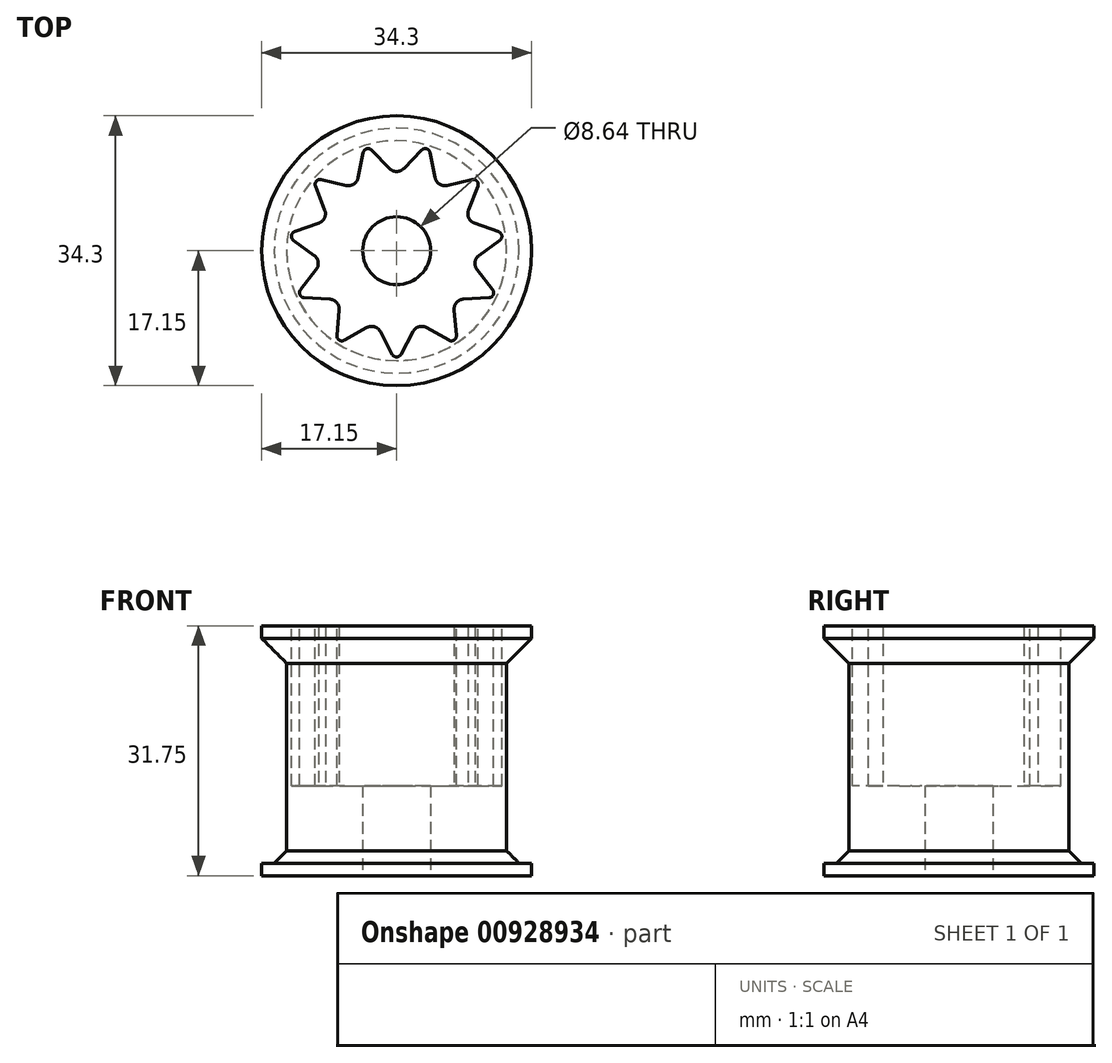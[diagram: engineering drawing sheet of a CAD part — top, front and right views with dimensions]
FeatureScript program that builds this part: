
annotation { "Feature Type Name" : "Feature", "Feature Type Description" : "" }
export const myFeature = defineFeature(function(context is Context, id is Id, definition is map)
    precondition{}
    {
        {
            var Q0;
            Q0=qCreatedBy(makeId("Top.planeOp"),FACE);
            var sketch = newSketch(context, id + "F0", { "sketchPlane" : qUnion([Q0])});
            skCircle(sketch, "E0", {"center": v(0, 0) * mm, "radius": 4.32 * mm});
            skCircle(sketch, "E1", {"center": v(0, 0) * mm, "radius": 12.7 * mm});
            skSolve(sketch);
        }
        {
            var Q0;
            Q0=makeQuery(id+"F0.imprint","IMPRINT",FACE,{"disambiguationData":[TD([[makeQuery(id+"F0.imprint","IMPRINT",EDGE,{"derivedFrom":sQuery(id+"F0.wireOp",EDGE,"E0")}),-1.0]])]});
            extrude(context, id + "F1", {"entities" : qUnion([Q0]), "depth" : 11.43 * mm, "offsetDistance" : 25.4 * mm});
        }
        {
            var Q0;
            Q0=qCreatedBy(makeId("Front.planeOp"),FACE);
            var sketch = newSketch(context, id + "F2", { "sketchPlane" : qUnion([Q0])});
            skLineSegment(sketch, "E2.bottom", {"start": v(0, 0) * mm, "end": v(-17.15, 0) * mm});
            skLineSegment(sketch, "E2.top", {"start": v(0, 0) * mm, "end": v(-17.15, 0) * mm});
            skLineSegment(sketch, "E2.left", {"start": v(0, 0) * mm, "end": v(0, 0) * mm});
            skLineSegment(sketch, "E2.right", {"start": v(-17.15, 0) * mm, "end": v(-17.15, 0) * mm});
            skLineSegment(sketch, "E3.top", {"start": v(-17.15, 1.59) * mm, "end": v(-17.15, 1.59) * mm});
            skLineSegment(sketch, "E3.left", {"start": v(-17.15, 0) * mm, "end": v(-17.15, 1.59) * mm});
            skLineSegment(sketch, "E3.right", {"start": v(-17.15, 0) * mm, "end": v(-17.15, 1.59) * mm});
            skLineSegment(sketch, "E4", {"start": v(-17.15, 1.59) * mm, "end": v(-13.97, 1.59) * mm});
            skLineSegment(sketch, "E5", {"start": v(-13.97, 1.59) * mm, "end": v(-13.97, 30.16) * mm});
            skLineSegment(sketch, "E6", {"start": v(-13.97, 30.16) * mm, "end": v(-17.15, 30.16) * mm});
            skLineSegment(sketch, "E7", {"start": v(-17.15, 30.16) * mm, "end": v(-17.15, 31.75) * mm});
            skLineSegment(sketch, "E8", {"start": v(-17.15, 31.75) * mm, "end": v(-10.8, 31.75) * mm});
            skLineSegment(sketch, "E9", {"start": v(0, 0) * mm, "end": v(-7.62, 0) * mm});
            skLineSegment(sketch, "E10", {"start": v(-7.62, 0) * mm, "end": v(-7.62, 1.59) * mm});
            skLineSegment(sketch, "E11", {"start": v(-7.62, 1.59) * mm, "end": v(-10.8, 1.59) * mm});
            skLineSegment(sketch, "E12", {"start": v(-10.8, 31.75) * mm, "end": v(-10.8, 1.59) * mm});
            skLineSegment(sketch, "E13", {"start": v(-17.15, 30.16) * mm, "end": v(-13.97, 26.99) * mm});
            skLineSegment(sketch, "E14", {"start": v(0, 0) * mm, "end": v(0, 23.16) * mm});
            skSolve(sketch);
        }
        {
            var Q0;
            {var subQ5=sQuery(id+"F2.wireOp",EDGE,"E3.left");Q0=makeQuery(id+"F2.imprint","IMPRINT",FACE,{"disambiguationData":[TD([[makeQuery(id+"F2.imprint","IMPRINT",EDGE,{"derivedFrom":subQ5}),-1.0]])]});}
            var Q1;
            {var subQ0=sQuery(id+"F2.wireOp",EDGE,"E6");Q1=makeQuery(id+"F2.imprint","IMPRINT",FACE,{"disambiguationData":[TD([[makeQuery(id+"F2.imprint","IMPRINT",EDGE,{"derivedFrom":subQ0}),1.0]])]});}
            var Q2;
            Q2=sQuery(id+"F2.wireOp",EDGE,"E14");
            revolve(context, id + "F3", {"operationType" : NewBodyOperationType.ADD, "surfaceOperationType" : NewSurfaceOperationType.NEW, "entities" : qUnion([Q0, Q1]), "axis" : qUnion([Q2]), "revolveType" : RevolveType.FULL});
        }
        {
            var Q0;
            Q0=makeQuery(id+"F1.opExtrude","CAP_FACE",FACE,{"disambiguationData":[OSD([sQuery(id+"F0.wireOp",EDGE,"E0"),sQuery(id+"F0.wireOp",EDGE,"E1")])],"isStart":false});
            var sketch = newSketch(context, id + "F4", { "sketchPlane" : qUnion([Q0])});
            skCircle(sketch, "E15", {"center": v(0, 0) * mm, "radius": 13.5 * mm});
            skLineSegment(sketch, "E16", {"start": v(0, 13.5) * mm, "end": v(0, 10.06) * mm});
            skArc(sketch, "E17", {"start": v(-0.91, 10.45) * mm, "mid": v(0, 10.06) * mm, "end": v(0.91, 10.45) * mm});
            skArc(sketch, "E18.1.0", {"start": v(-6.42, 8.3) * mm, "mid": v(-5.44, 8.47) * mm, "end": v(-4.88, 9.29) * mm});
            skArc(sketch, "E18.2.0", {"start": v(-9.89, 3.51) * mm, "mid": v(-9.16, 4.18) * mm, "end": v(-9.13, 5.17) * mm});
            skArc(sketch, "E18.3.0", {"start": v(-10.22, -2.4) * mm, "mid": v(-9.96, -1.43) * mm, "end": v(-10.47, -0.58) * mm});
            skArc(sketch, "E18.4.0", {"start": v(-7.3, -7.53) * mm, "mid": v(-7.6, -6.6) * mm, "end": v(-8.5, -6.15) * mm});
            skArc(sketch, "E18.5.0", {"start": v(-2.07, -10.29) * mm, "mid": v(-2.84, -9.66) * mm, "end": v(-3.82, -9.77) * mm});
            skArc(sketch, "E18.6.0", {"start": v(3.82, -9.77) * mm, "mid": v(2.84, -9.66) * mm, "end": v(2.07, -10.29) * mm});
            skArc(sketch, "E18.7.0", {"start": v(8.5, -6.15) * mm, "mid": v(7.6, -6.6) * mm, "end": v(7.3, -7.53) * mm});
            skArc(sketch, "E18.8.0", {"start": v(10.47, -0.58) * mm, "mid": v(9.96, -1.43) * mm, "end": v(10.22, -2.4) * mm});
            skArc(sketch, "E18.9.0", {"start": v(9.13, 5.17) * mm, "mid": v(9.16, 4.18) * mm, "end": v(9.89, 3.51) * mm});
            skArc(sketch, "E18.10.0", {"start": v(4.88, 9.29) * mm, "mid": v(5.44, 8.47) * mm, "end": v(6.42, 8.3) * mm});
            skLineSegment(sketch, "E19", {"start": v(0, 0) * mm, "end": v(3.8, 12.95) * mm});
            skCircle(sketch, "E20", {"center": v(3.62, 12.34) * mm, "radius": 0.64 * mm});
            skCircle(sketch, "E21.1.0", {"center": v(-3.62, 12.34) * mm, "radius": 0.64 * mm});
            skCircle(sketch, "E21.2.0", {"center": v(-9.72, 8.42) * mm, "radius": 0.64 * mm});
            skCircle(sketch, "E22.1.3.0", {"center": v(-12.73, 1.83) * mm, "radius": 0.64 * mm});
            skCircle(sketch, "E22.1.4.0", {"center": v(-11.7, -5.34) * mm, "radius": 0.64 * mm});
            skCircle(sketch, "E22.1.5.0", {"center": v(-6.95, -10.82) * mm, "radius": 0.64 * mm});
            skCircle(sketch, "E22.1.6.0", {"center": v(0, -12.86) * mm, "radius": 0.64 * mm});
            skCircle(sketch, "E22.1.7.0", {"center": v(6.95, -10.82) * mm, "radius": 0.64 * mm});
            skCircle(sketch, "E22.1.8.0", {"center": v(11.7, -5.34) * mm, "radius": 0.64 * mm});
            skCircle(sketch, "E22.1.9.0", {"center": v(12.73, 1.83) * mm, "radius": 0.64 * mm});
            skCircle(sketch, "E22.1.10.0", {"center": v(9.72, 8.42) * mm, "radius": 0.64 * mm});
            skLineSegment(sketch, "E23", {"start": v(-9.13, 5.17) * mm, "end": v(-10.3, 8.19) * mm});
            skLineSegment(sketch, "E24", {"start": v(-9.89, 3.51) * mm, "end": v(-12.94, 2.43) * mm});
            skLineSegment(sketch, "E25", {"start": v(-9.57, 9.04) * mm, "end": v(-6.42, 8.3) * mm});
            skLineSegment(sketch, "E26", {"start": v(-13.1, 1.32) * mm, "end": v(-10.47, -0.58) * mm});
            skLineSegment(sketch, "E27", {"start": v(-10.22, -2.4) * mm, "end": v(-12.2, -4.95) * mm});
            skLineSegment(sketch, "E28", {"start": v(-7.3, -7.53) * mm, "end": v(-7.58, -10.76) * mm});
            skLineSegment(sketch, "E29", {"start": v(-6.64, -11.37) * mm, "end": v(-3.82, -9.77) * mm});
            skLineSegment(sketch, "E30", {"start": v(-2.07, -10.29) * mm, "end": v(-0.56, -13.15) * mm});
            skLineSegment(sketch, "E31", {"start": v(0.56, -13.15) * mm, "end": v(2.07, -10.29) * mm});
            skLineSegment(sketch, "E32", {"start": v(3.82, -9.77) * mm, "end": v(6.64, -11.37) * mm});
            skLineSegment(sketch, "E33", {"start": v(7.58, -10.76) * mm, "end": v(7.3, -7.53) * mm});
            skLineSegment(sketch, "E34", {"start": v(8.5, -6.15) * mm, "end": v(11.73, -5.98) * mm});
            skLineSegment(sketch, "E35", {"start": v(-4.88, 9.29) * mm, "end": v(-4.25, 12.46) * mm});
            skLineSegment(sketch, "E36", {"start": v(-3.17, 12.78) * mm, "end": v(-0.91, 10.45) * mm});
            skLineSegment(sketch, "E37", {"start": v(0.91, 10.45) * mm, "end": v(3.17, 12.78) * mm});
            skLineSegment(sketch, "E38", {"start": v(10.3, 8.19) * mm, "end": v(9.13, 5.17) * mm});
            skLineSegment(sketch, "E39", {"start": v(9.89, 3.51) * mm, "end": v(12.94, 2.43) * mm});
            skLineSegment(sketch, "E40", {"start": v(13.1, 1.32) * mm, "end": v(10.47, -0.58) * mm});
            skLineSegment(sketch, "E41", {"start": v(10.22, -2.4) * mm, "end": v(12.2, -4.95) * mm});
            skLineSegment(sketch, "E42", {"start": v(4.25, 12.46) * mm, "end": v(4.88, 9.29) * mm});
            skLineSegment(sketch, "E43", {"start": v(6.42, 8.3) * mm, "end": v(9.57, 9.04) * mm});
            skLineSegment(sketch, "E44", {"start": v(-11.73, -5.98) * mm, "end": v(-8.5, -6.15) * mm});
            skCircle(sketch, "E45", {"center": v(0, 0) * mm, "radius": 15.88 * mm});
            skSolve(sketch);
        }
        {
            var Q0;
            Q0=makeQuery(id+"F3.opRevolve","SWEPT_EDGE",EDGE,{"disambiguationData":[OSD([sQuery(id+"F2.wireOp",EDGE,"E4"),sQuery(id+"F2.wireOp",EDGE,"E5")])]});
            chamfer(context, id + "F5", {"entities" : qUnion([Q0]), "width" : 1.59 * mm, "tangentPropagation" : true});
        }
        {
            var Q0;
            Q0=makeQuery(id+"F3.opRevolve","SWEPT_FACE",FACE,{"disambiguationData":[OSD([sQuery(id+"F2.wireOp",EDGE,"E8")])]});
            var sketch = newSketch(context, id + "F6", { "sketchPlane" : qUnion([Q0])});
            skCircle(sketch, "E46", {"center": v(0, 0) * mm, "radius": 13.5 * mm});
            skLineSegment(sketch, "E47", {"start": v(0, 13.5) * mm, "end": v(0, 10.06) * mm});
            skCircle(sketch, "E48", {"center": v(0, 11.33) * mm, "radius": 1.27 * mm});
            skCircle(sketch, "E49.1.0", {"center": v(-6.13, 9.54) * mm, "radius": 1.27 * mm});
            skCircle(sketch, "E49.2.0", {"center": v(-10.31, 4.7) * mm, "radius": 1.27 * mm});
            skCircle(sketch, "E49.3.0", {"center": v(-11.22, -1.61) * mm, "radius": 1.27 * mm});
            skCircle(sketch, "E49.4.0", {"center": v(-8.57, -7.42) * mm, "radius": 1.27 * mm});
            skCircle(sketch, "E49.5.0", {"center": v(-3.2, -10.88) * mm, "radius": 1.27 * mm});
            skCircle(sketch, "E49.6.0", {"center": v(3.2, -10.88) * mm, "radius": 1.27 * mm});
            skCircle(sketch, "E49.7.0", {"center": v(8.57, -7.42) * mm, "radius": 1.27 * mm});
            skCircle(sketch, "E49.8.0", {"center": v(11.22, -1.61) * mm, "radius": 1.27 * mm});
            skCircle(sketch, "E49.9.0", {"center": v(10.31, 4.7) * mm, "radius": 1.27 * mm});
            skCircle(sketch, "E49.10.0", {"center": v(6.13, 9.54) * mm, "radius": 1.27 * mm});
            skLineSegment(sketch, "E50", {"start": v(0, 0) * mm, "end": v(3.8, 12.95) * mm});
            skCircle(sketch, "E51", {"center": v(3.62, 12.34) * mm, "radius": 0.64 * mm});
            skCircle(sketch, "E52.1.0", {"center": v(-3.62, 12.34) * mm, "radius": 0.64 * mm});
            skCircle(sketch, "E52.2.0", {"center": v(-9.72, 8.42) * mm, "radius": 0.64 * mm});
            skCircle(sketch, "E53.1.3.0", {"center": v(-12.73, 1.83) * mm, "radius": 0.64 * mm});
            skCircle(sketch, "E53.1.4.0", {"center": v(-11.7, -5.34) * mm, "radius": 0.64 * mm});
            skCircle(sketch, "E53.1.5.0", {"center": v(-6.95, -10.82) * mm, "radius": 0.64 * mm});
            skCircle(sketch, "E53.1.6.0", {"center": v(0, -12.86) * mm, "radius": 0.64 * mm});
            skCircle(sketch, "E53.1.7.0", {"center": v(6.95, -10.82) * mm, "radius": 0.64 * mm});
            skCircle(sketch, "E53.1.8.0", {"center": v(11.7, -5.34) * mm, "radius": 0.64 * mm});
            skCircle(sketch, "E53.1.9.0", {"center": v(12.73, 1.83) * mm, "radius": 0.64 * mm});
            skCircle(sketch, "E53.1.10.0", {"center": v(9.72, 8.42) * mm, "radius": 0.64 * mm});
            skLineSegment(sketch, "E54", {"start": v(-9.13, 5.17) * mm, "end": v(-10.3, 8.19) * mm});
            skLineSegment(sketch, "E55", {"start": v(-9.89, 3.51) * mm, "end": v(-12.94, 2.43) * mm});
            skLineSegment(sketch, "E56", {"start": v(-9.57, 9.04) * mm, "end": v(-6.42, 8.3) * mm});
            skLineSegment(sketch, "E57", {"start": v(-13.1, 1.32) * mm, "end": v(-10.47, -0.58) * mm});
            skLineSegment(sketch, "E58", {"start": v(-10.22, -2.4) * mm, "end": v(-12.2, -4.95) * mm});
            skLineSegment(sketch, "E59", {"start": v(-7.3, -7.53) * mm, "end": v(-7.58, -10.76) * mm});
            skLineSegment(sketch, "E60", {"start": v(-6.64, -11.37) * mm, "end": v(-3.82, -9.77) * mm});
            skLineSegment(sketch, "E61", {"start": v(-2.07, -10.29) * mm, "end": v(-0.56, -13.15) * mm});
            skLineSegment(sketch, "E62", {"start": v(0.56, -13.15) * mm, "end": v(2.07, -10.29) * mm});
            skLineSegment(sketch, "E63", {"start": v(3.82, -9.77) * mm, "end": v(6.64, -11.37) * mm});
            skLineSegment(sketch, "E64", {"start": v(7.58, -10.76) * mm, "end": v(7.3, -7.53) * mm});
            skLineSegment(sketch, "E65", {"start": v(8.5, -6.15) * mm, "end": v(11.73, -5.98) * mm});
            skLineSegment(sketch, "E66", {"start": v(-4.88, 9.29) * mm, "end": v(-4.25, 12.46) * mm});
            skLineSegment(sketch, "E67", {"start": v(-3.17, 12.78) * mm, "end": v(-0.91, 10.45) * mm});
            skLineSegment(sketch, "E68", {"start": v(0.91, 10.45) * mm, "end": v(3.17, 12.78) * mm});
            skLineSegment(sketch, "E69", {"start": v(10.3, 8.19) * mm, "end": v(9.13, 5.17) * mm});
            skLineSegment(sketch, "E70", {"start": v(9.89, 3.51) * mm, "end": v(12.94, 2.43) * mm});
            skLineSegment(sketch, "E71", {"start": v(13.1, 1.32) * mm, "end": v(10.47, -0.58) * mm});
            skLineSegment(sketch, "E72", {"start": v(10.22, -2.4) * mm, "end": v(12.2, -4.95) * mm});
            skLineSegment(sketch, "E73", {"start": v(4.25, 12.46) * mm, "end": v(4.88, 9.29) * mm});
            skLineSegment(sketch, "E74", {"start": v(6.42, 8.3) * mm, "end": v(9.57, 9.04) * mm});
            skLineSegment(sketch, "E75", {"start": v(-11.73, -5.98) * mm, "end": v(-8.5, -6.15) * mm});
            skCircle(sketch, "E76", {"center": v(0, 0) * mm, "radius": 15.88 * mm});
            skSolve(sketch);
        }
        {
            var Q0;
            {var subQ0=sQuery(id+"F6.wireOp",EDGE,"E58");var subQ1=sQuery(id+"F6.wireOp",EDGE,"E53.1.4.0");var subQ2=makeQuery(id+"F6.imprint","INTERSECT",VERTEX,{"derivedFrom":[subQ1,subQ0]});Q0=makeQuery(id+"F6.imprint","IMPRINT",FACE,{"disambiguationData":[TD([[makeQuery(id+"F6.imprint","IMPRINT",EDGE,{"disambiguationData":[TD([[subQ2,1.0]])],"derivedFrom":subQ1}),-1.0]])]});}
            var Q1;
            {var subQ0=sQuery(id+"F6.wireOp",EDGE,"E53.1.4.0");var subQ1=makeQuery(id+"F6.imprint","INTERSECT",VERTEX,{"derivedFrom":[subQ0,sQuery(id+"F6.wireOp",EDGE,"E58")]});Q1=makeQuery(id+"F6.imprint","IMPRINT",FACE,{"disambiguationData":[TD([[makeQuery(id+"F6.imprint","IMPRINT",EDGE,{"disambiguationData":[TD([[subQ1,-1.0]])],"derivedFrom":subQ0}),1.0]])]});}
            var Q2;
            {var subQ0=sQuery(id+"F6.wireOp",EDGE,"E55");var subQ1=sQuery(id+"F6.wireOp",EDGE,"E53.1.3.0");var subQ2=makeQuery(id+"F6.imprint","INTERSECT",VERTEX,{"derivedFrom":[subQ1,subQ0]});Q2=makeQuery(id+"F6.imprint","IMPRINT",FACE,{"disambiguationData":[TD([[makeQuery(id+"F6.imprint","IMPRINT",EDGE,{"disambiguationData":[TD([[subQ2,1.0]])],"derivedFrom":subQ1}),-1.0]])]});}
            var Q3;
            {var subQ0=sQuery(id+"F6.wireOp",EDGE,"E53.1.3.0");var subQ1=makeQuery(id+"F6.imprint","INTERSECT",VERTEX,{"derivedFrom":[subQ0,sQuery(id+"F6.wireOp",EDGE,"E55")]});Q3=makeQuery(id+"F6.imprint","IMPRINT",FACE,{"disambiguationData":[TD([[makeQuery(id+"F6.imprint","IMPRINT",EDGE,{"disambiguationData":[TD([[subQ1,-1.0]])],"derivedFrom":subQ0}),1.0]])]});}
            var Q4;
            {var subQ0=sQuery(id+"F6.wireOp",EDGE,"E54");var subQ1=sQuery(id+"F6.wireOp",EDGE,"E52.2.0");var subQ2=makeQuery(id+"F6.imprint","INTERSECT",VERTEX,{"derivedFrom":[subQ1,subQ0]});Q4=makeQuery(id+"F6.imprint","IMPRINT",FACE,{"disambiguationData":[TD([[makeQuery(id+"F6.imprint","IMPRINT",EDGE,{"disambiguationData":[TD([[subQ2,-1.0]])],"derivedFrom":subQ1}),-1.0]])]});}
            var Q5;
            {var subQ0=sQuery(id+"F6.wireOp",EDGE,"E52.2.0");var subQ1=makeQuery(id+"F6.imprint","INTERSECT",VERTEX,{"derivedFrom":[subQ0,sQuery(id+"F6.wireOp",EDGE,"E56")]});Q5=makeQuery(id+"F6.imprint","IMPRINT",FACE,{"disambiguationData":[TD([[makeQuery(id+"F6.imprint","IMPRINT",EDGE,{"disambiguationData":[TD([[subQ1,-1.0]])],"derivedFrom":subQ0}),1.0]])]});}
            var Q6;
            {var subQ0=sQuery(id+"F6.wireOp",EDGE,"E66");var subQ1=sQuery(id+"F6.wireOp",EDGE,"E52.1.0");var subQ2=makeQuery(id+"F6.imprint","INTERSECT",VERTEX,{"derivedFrom":[subQ1,subQ0]});Q6=makeQuery(id+"F6.imprint","IMPRINT",FACE,{"disambiguationData":[TD([[makeQuery(id+"F6.imprint","IMPRINT",EDGE,{"disambiguationData":[TD([[subQ2,-1.0]])],"derivedFrom":subQ1}),-1.0]])]});}
            var Q7;
            {var subQ0=sQuery(id+"F6.wireOp",EDGE,"E52.1.0");var subQ1=makeQuery(id+"F6.imprint","INTERSECT",VERTEX,{"derivedFrom":[subQ0,sQuery(id+"F6.wireOp",EDGE,"E67")]});Q7=makeQuery(id+"F6.imprint","IMPRINT",FACE,{"disambiguationData":[TD([[makeQuery(id+"F6.imprint","IMPRINT",EDGE,{"disambiguationData":[TD([[subQ1,-1.0]])],"derivedFrom":subQ0}),1.0]])]});}
            var Q8;
            {var subQ0=sQuery(id+"F6.wireOp",EDGE,"E51");var subQ5=sQuery(id+"F6.wireOp",EDGE,"E68");var subQ6=makeQuery(id+"F6.imprint","INTERSECT",VERTEX,{"derivedFrom":[subQ0,subQ5]});Q8=makeQuery(id+"F6.imprint","IMPRINT",FACE,{"disambiguationData":[TD([[makeQuery(id+"F6.imprint","IMPRINT",EDGE,{"disambiguationData":[TD([[subQ6,-1.0]])],"derivedFrom":subQ0}),-1.0]])]});}
            var Q9;
            {var subQ0=sQuery(id+"F6.wireOp",EDGE,"E51");var subQ4=makeQuery(id+"F6.imprint","INTERSECT",VERTEX,{"derivedFrom":[subQ0,sQuery(id+"F6.wireOp",EDGE,"E73")]});Q9=makeQuery(id+"F6.imprint","IMPRINT",FACE,{"disambiguationData":[TD([[makeQuery(id+"F6.imprint","IMPRINT",EDGE,{"disambiguationData":[TD([[subQ4,1.0]])],"derivedFrom":subQ0}),1.0]])]});}
            var Q10;
            {var subQ0=sQuery(id+"F6.wireOp",EDGE,"E51");var subQ5=sQuery(id+"F6.wireOp",EDGE,"E73");var subQ6=makeQuery(id+"F6.imprint","INTERSECT",VERTEX,{"derivedFrom":[subQ0,subQ5]});Q10=makeQuery(id+"F6.imprint","IMPRINT",FACE,{"disambiguationData":[TD([[makeQuery(id+"F6.imprint","IMPRINT",EDGE,{"disambiguationData":[TD([[subQ6,1.0]])],"derivedFrom":subQ0}),-1.0]])]});}
            var Q11;
            {var subQ0=sQuery(id+"F6.wireOp",EDGE,"E51");var subQ4=makeQuery(id+"F6.imprint","INTERSECT",VERTEX,{"derivedFrom":[subQ0,sQuery(id+"F6.wireOp",EDGE,"E68")]});Q11=makeQuery(id+"F6.imprint","IMPRINT",FACE,{"disambiguationData":[TD([[makeQuery(id+"F6.imprint","IMPRINT",EDGE,{"disambiguationData":[TD([[subQ4,-1.0]])],"derivedFrom":subQ0}),1.0]])]});}
            var Q12;
            {var subQ0=sQuery(id+"F6.wireOp",EDGE,"E59");var subQ1=sQuery(id+"F6.wireOp",EDGE,"E53.1.5.0");var subQ2=makeQuery(id+"F6.imprint","INTERSECT",VERTEX,{"derivedFrom":[subQ1,subQ0]});Q12=makeQuery(id+"F6.imprint","IMPRINT",FACE,{"disambiguationData":[TD([[makeQuery(id+"F6.imprint","IMPRINT",EDGE,{"disambiguationData":[TD([[subQ2,1.0]])],"derivedFrom":subQ1}),-1.0]])]});}
            var Q13;
            {var subQ0=sQuery(id+"F6.wireOp",EDGE,"E53.1.5.0");var subQ1=makeQuery(id+"F6.imprint","INTERSECT",VERTEX,{"derivedFrom":[subQ0,sQuery(id+"F6.wireOp",EDGE,"E59")]});Q13=makeQuery(id+"F6.imprint","IMPRINT",FACE,{"disambiguationData":[TD([[makeQuery(id+"F6.imprint","IMPRINT",EDGE,{"disambiguationData":[TD([[subQ1,-1.0]])],"derivedFrom":subQ0}),1.0]])]});}
            var Q14;
            {var subQ0=sQuery(id+"F6.wireOp",EDGE,"E61");var subQ1=sQuery(id+"F6.wireOp",EDGE,"E53.1.6.0");var subQ2=makeQuery(id+"F6.imprint","INTERSECT",VERTEX,{"derivedFrom":[subQ1,subQ0]});Q14=makeQuery(id+"F6.imprint","IMPRINT",FACE,{"disambiguationData":[TD([[makeQuery(id+"F6.imprint","IMPRINT",EDGE,{"disambiguationData":[TD([[subQ2,1.0]])],"derivedFrom":subQ1}),-1.0]])]});}
            var Q15;
            {var subQ0=sQuery(id+"F6.wireOp",EDGE,"E53.1.6.0");var subQ1=makeQuery(id+"F6.imprint","INTERSECT",VERTEX,{"derivedFrom":[subQ0,sQuery(id+"F6.wireOp",EDGE,"E61")]});Q15=makeQuery(id+"F6.imprint","IMPRINT",FACE,{"disambiguationData":[TD([[makeQuery(id+"F6.imprint","IMPRINT",EDGE,{"disambiguationData":[TD([[subQ1,-1.0]])],"derivedFrom":subQ0}),1.0]])]});}
            var Q16;
            {var subQ0=sQuery(id+"F6.wireOp",EDGE,"E63");var subQ1=sQuery(id+"F6.wireOp",EDGE,"E53.1.7.0");var subQ2=makeQuery(id+"F6.imprint","INTERSECT",VERTEX,{"derivedFrom":[subQ1,subQ0]});Q16=makeQuery(id+"F6.imprint","IMPRINT",FACE,{"disambiguationData":[TD([[makeQuery(id+"F6.imprint","IMPRINT",EDGE,{"disambiguationData":[TD([[subQ2,1.0]])],"derivedFrom":subQ1}),-1.0]])]});}
            var Q17;
            {var subQ0=sQuery(id+"F6.wireOp",EDGE,"E53.1.7.0");var subQ1=makeQuery(id+"F6.imprint","INTERSECT",VERTEX,{"derivedFrom":[subQ0,sQuery(id+"F6.wireOp",EDGE,"E63")]});Q17=makeQuery(id+"F6.imprint","IMPRINT",FACE,{"disambiguationData":[TD([[makeQuery(id+"F6.imprint","IMPRINT",EDGE,{"disambiguationData":[TD([[subQ1,-1.0]])],"derivedFrom":subQ0}),1.0]])]});}
            var Q18;
            {var subQ0=sQuery(id+"F6.wireOp",EDGE,"E65");var subQ1=sQuery(id+"F6.wireOp",EDGE,"E53.1.8.0");var subQ2=makeQuery(id+"F6.imprint","INTERSECT",VERTEX,{"derivedFrom":[subQ1,subQ0]});Q18=makeQuery(id+"F6.imprint","IMPRINT",FACE,{"disambiguationData":[TD([[makeQuery(id+"F6.imprint","IMPRINT",EDGE,{"disambiguationData":[TD([[subQ2,1.0]])],"derivedFrom":subQ1}),-1.0]])]});}
            var Q19;
            {var subQ0=sQuery(id+"F6.wireOp",EDGE,"E53.1.8.0");var subQ1=makeQuery(id+"F6.imprint","INTERSECT",VERTEX,{"derivedFrom":[subQ0,sQuery(id+"F6.wireOp",EDGE,"E65")]});Q19=makeQuery(id+"F6.imprint","IMPRINT",FACE,{"disambiguationData":[TD([[makeQuery(id+"F6.imprint","IMPRINT",EDGE,{"disambiguationData":[TD([[subQ1,-1.0]])],"derivedFrom":subQ0}),1.0]])]});}
            var Q20;
            {var subQ0=sQuery(id+"F6.wireOp",EDGE,"E70");var subQ1=sQuery(id+"F6.wireOp",EDGE,"E53.1.9.0");var subQ2=makeQuery(id+"F6.imprint","INTERSECT",VERTEX,{"derivedFrom":[subQ1,subQ0]});Q20=makeQuery(id+"F6.imprint","IMPRINT",FACE,{"disambiguationData":[TD([[makeQuery(id+"F6.imprint","IMPRINT",EDGE,{"disambiguationData":[TD([[subQ2,-1.0]])],"derivedFrom":subQ1}),-1.0]])]});}
            var Q21;
            {var subQ0=sQuery(id+"F6.wireOp",EDGE,"E53.1.9.0");var subQ1=makeQuery(id+"F6.imprint","INTERSECT",VERTEX,{"derivedFrom":[subQ0,sQuery(id+"F6.wireOp",EDGE,"E71")]});Q21=makeQuery(id+"F6.imprint","IMPRINT",FACE,{"disambiguationData":[TD([[makeQuery(id+"F6.imprint","IMPRINT",EDGE,{"disambiguationData":[TD([[subQ1,-1.0]])],"derivedFrom":subQ0}),1.0]])]});}
            var Q22;
            {var subQ0=sQuery(id+"F6.wireOp",EDGE,"E69");var subQ1=sQuery(id+"F6.wireOp",EDGE,"E53.1.10.0");var subQ2=makeQuery(id+"F6.imprint","INTERSECT",VERTEX,{"derivedFrom":[subQ1,subQ0]});Q22=makeQuery(id+"F6.imprint","IMPRINT",FACE,{"disambiguationData":[TD([[makeQuery(id+"F6.imprint","IMPRINT",EDGE,{"disambiguationData":[TD([[subQ2,1.0]])],"derivedFrom":subQ1}),-1.0]])]});}
            var Q23;
            {var subQ0=sQuery(id+"F6.wireOp",EDGE,"E53.1.10.0");var subQ1=makeQuery(id+"F6.imprint","INTERSECT",VERTEX,{"derivedFrom":[subQ0,sQuery(id+"F6.wireOp",EDGE,"E69")]});Q23=makeQuery(id+"F6.imprint","IMPRINT",FACE,{"disambiguationData":[TD([[makeQuery(id+"F6.imprint","IMPRINT",EDGE,{"disambiguationData":[TD([[subQ1,-1.0]])],"derivedFrom":subQ0}),1.0]])]});}
            var Q24;
            Q24=sQuery(id+"F4.wireOp",VERTEX,"E29.end");
            extrude(context, id + "F7", {"entities" : qUnion([Q0, Q1, Q2, Q3, Q4, Q5, Q6, Q7, Q8, Q9, Q10, Q11, Q12, Q13, Q14, Q15, Q16, Q17, Q18, Q19, Q20, Q21, Q22, Q23]), "operationType" : NewBodyOperationType.REMOVE, "endBound" : BoundingType.UP_TO_VERTEX, "oppositeDirection" : true, "depth" : 25.4 * mm, "endBoundEntityVertex" : qUnion([Q24]), "offsetDistance" : 25.4 * mm});
        }
        {
            var Q0;
            {var subQ0=sQuery(id+"F4.wireOp",EDGE,"E18.9.0");Q0=makeQuery(id+"F4.imprint","IMPRINT",FACE,{"disambiguationData":[TD([[makeQuery(id+"F4.imprint","IMPRINT",EDGE,{"derivedFrom":subQ0}),1.0]])]});}
            var Q1;
            {var subQ0=sQuery(id+"F4.wireOp",EDGE,"E18.8.0");Q1=makeQuery(id+"F4.imprint","IMPRINT",FACE,{"disambiguationData":[TD([[makeQuery(id+"F4.imprint","IMPRINT",EDGE,{"derivedFrom":subQ0}),1.0]])]});}
            var Q2;
            {var subQ0=sQuery(id+"F4.wireOp",EDGE,"E18.7.0");Q2=makeQuery(id+"F4.imprint","IMPRINT",FACE,{"disambiguationData":[TD([[makeQuery(id+"F4.imprint","IMPRINT",EDGE,{"derivedFrom":subQ0}),1.0]])]});}
            var Q3;
            {var subQ0=sQuery(id+"F4.wireOp",EDGE,"E18.6.0");Q3=makeQuery(id+"F4.imprint","IMPRINT",FACE,{"disambiguationData":[TD([[makeQuery(id+"F4.imprint","IMPRINT",EDGE,{"derivedFrom":subQ0}),1.0]])]});}
            var Q4;
            {var subQ0=sQuery(id+"F4.wireOp",EDGE,"E18.5.0");Q4=makeQuery(id+"F4.imprint","IMPRINT",FACE,{"disambiguationData":[TD([[makeQuery(id+"F4.imprint","IMPRINT",EDGE,{"derivedFrom":subQ0}),1.0]])]});}
            var Q5;
            {var subQ0=sQuery(id+"F4.wireOp",EDGE,"E18.4.0");Q5=makeQuery(id+"F4.imprint","IMPRINT",FACE,{"disambiguationData":[TD([[makeQuery(id+"F4.imprint","IMPRINT",EDGE,{"derivedFrom":subQ0}),1.0]])]});}
            var Q6;
            {var subQ0=sQuery(id+"F4.wireOp",EDGE,"E18.3.0");Q6=makeQuery(id+"F4.imprint","IMPRINT",FACE,{"disambiguationData":[TD([[makeQuery(id+"F4.imprint","IMPRINT",EDGE,{"derivedFrom":subQ0}),1.0]])]});}
            var Q7;
            {var subQ0=sQuery(id+"F4.wireOp",EDGE,"E18.2.0");Q7=makeQuery(id+"F4.imprint","IMPRINT",FACE,{"disambiguationData":[TD([[makeQuery(id+"F4.imprint","IMPRINT",EDGE,{"derivedFrom":subQ0}),1.0]])]});}
            var Q8;
            {var subQ0=sQuery(id+"F4.wireOp",EDGE,"E18.1.0");Q8=makeQuery(id+"F4.imprint","IMPRINT",FACE,{"disambiguationData":[TD([[makeQuery(id+"F4.imprint","IMPRINT",EDGE,{"derivedFrom":subQ0}),1.0]])]});}
            var Q9;
            {var subQ0=sQuery(id+"F4.wireOp",EDGE,"E17");var subQ1=sQuery(id+"F4.wireOp",EDGE,"E16");var subQ2=makeQuery(id+"F4.imprint","INTERSECT",VERTEX,{"derivedFrom":[subQ1,subQ0]});Q9=makeQuery(id+"F4.imprint","IMPRINT",FACE,{"disambiguationData":[TD([[makeQuery(id+"F4.imprint","IMPRINT",EDGE,{"disambiguationData":[TD([[subQ2,1.0]])],"derivedFrom":subQ0}),1.0]])]});}
            var Q10;
            {var subQ0=sQuery(id+"F4.wireOp",EDGE,"E17");var subQ1=sQuery(id+"F4.wireOp",EDGE,"E16");var subQ2=makeQuery(id+"F4.imprint","INTERSECT",VERTEX,{"derivedFrom":[subQ1,subQ0]});Q10=makeQuery(id+"F4.imprint","IMPRINT",FACE,{"disambiguationData":[TD([[makeQuery(id+"F4.imprint","IMPRINT",EDGE,{"disambiguationData":[TD([[subQ2,-1.0]])],"derivedFrom":subQ0}),1.0]])]});}
            var Q11;
            {var subQ0=sQuery(id+"F4.wireOp",EDGE,"E18.10.0");Q11=makeQuery(id+"F4.imprint","IMPRINT",FACE,{"disambiguationData":[TD([[makeQuery(id+"F4.imprint","IMPRINT",EDGE,{"derivedFrom":subQ0}),1.0]])]});}
            var Q12;
            Q12=makeQuery(id+"F7.boolean.opBoolean","COPY",VERTEX,{"derivedFrom":makeQuery(id+"F7.opExtrude","CAP_VERTEX",VERTEX,{"disambiguationData":[OSD([sQuery(id+"F2.wireOp",EDGE,"E8"),sQuery(id+"F2.wireOp",EDGE,"E12"),sQuery(id+"F6.wireOp",EDGE,"E74")])],"isStart":true})});
            extrude(context, id + "F8", {"entities" : qUnion([Q0, Q1, Q2, Q3, Q4, Q5, Q6, Q7, Q8, Q9, Q10, Q11]), "operationType" : NewBodyOperationType.ADD, "endBound" : BoundingType.UP_TO_VERTEX, "depth" : 25.4 * mm, "endBoundEntityVertex" : qUnion([Q12]), "offsetDistance" : 25.4 * mm});
        }
    });
